# Revit family: Sanitary_Taps&Mixers_Zurn_Z82300-XL
name_source: partatom
category: Plumbing Fixtures
units: mm (PartAtom-declared; Revit-internal decimal feet)

## family parameters
Cut with Voids When Loaded = No
Host = Face
Maintain Annotation Orientation = No
OmniClass Number = 23.45.55.17
OmniClass Title = Mixing Faucets
Part Type = Normal
Room Calculation Point = No
Round Connector Dimension = Use Radius
Shared = No

## types (8) — shared parameters
Assembly Code = D2010.60
CW Connection = Yes
CWFU = 1
Cold Inlet Connection Size (inch) = 0.5 "
Default Elevation = 34 "
Description = SINGLE CONTROL FAUCET
Disnace B/w Fixture to Spout with handle = 5.875 "
Distance B/W Base & Aerator = 4.5 "
Distance b/w spout axis to aerator Axis = 10 "
HW Connection = Yes
HWFU = 1
Handle length = 4 "
Hot Inlet Connection Size (inch) = 0.5 "
Main Material = Chrome-Plated Brass - Zurn - Polished
Manufacturer = Zurn Industries, LLC
Manufacturer Brand = Zurn
Model = Z82300-XL
Modified date = 10/06/2025
Product Documentation Link = https://files.zurn.com
Product Installation Sheet URL = https://files.zurn.com
Product Page URL = https://www.zurn.com
Product data url = https://www.bimobject.com
Repair Parts URL = https://files.zurn.com
Spout Base Width = 2.125 "
Spout Reach = 4.5 "
URL = http://www.zurn.com
Vent Connection = No
Waste Connection = No
zero-valued in all types: WFU

## per-type parameters (varying)
| type | Flow Rate | Type of Outlet |
| Z82300-XL-2M (2.2 GPM AERATOR OUTLET) | 2 GPM | AERATOR |
| Z82300-XL-3M (0.5 GPM SPRAY OUTLET) | 1 GPM | SPRAY |
| Z82300-XL-4M (2.2 GPM LAMINAR OUTLET) | 2 GPM | LAMINAR |
| Z82300-XL-7M (1.0 GPM SPRAY OUTLET) | 1 GPM | SPRAY |
| Z82300-XL-16M (1.0 GPM SPRAY OUTLET) | 1 GPM | SPRAY |
| Z82300-XL-17M (1.5 GPM AERATOR OUTLET) | 2 GPM | AERATOR |
| Z82300-XL-18M (1.5 GPM LAMINAR OUTLET) | 2 GPM | LAMINAR |
| Z82300-XL-22M (1.0 GPM LAMINAR OUTLET) | 1 GPM | LAMINAR |

## geometry (parser evidence)
native form markers: Blend x4, Sweep x4
no freeform markers — native parametric forms only
